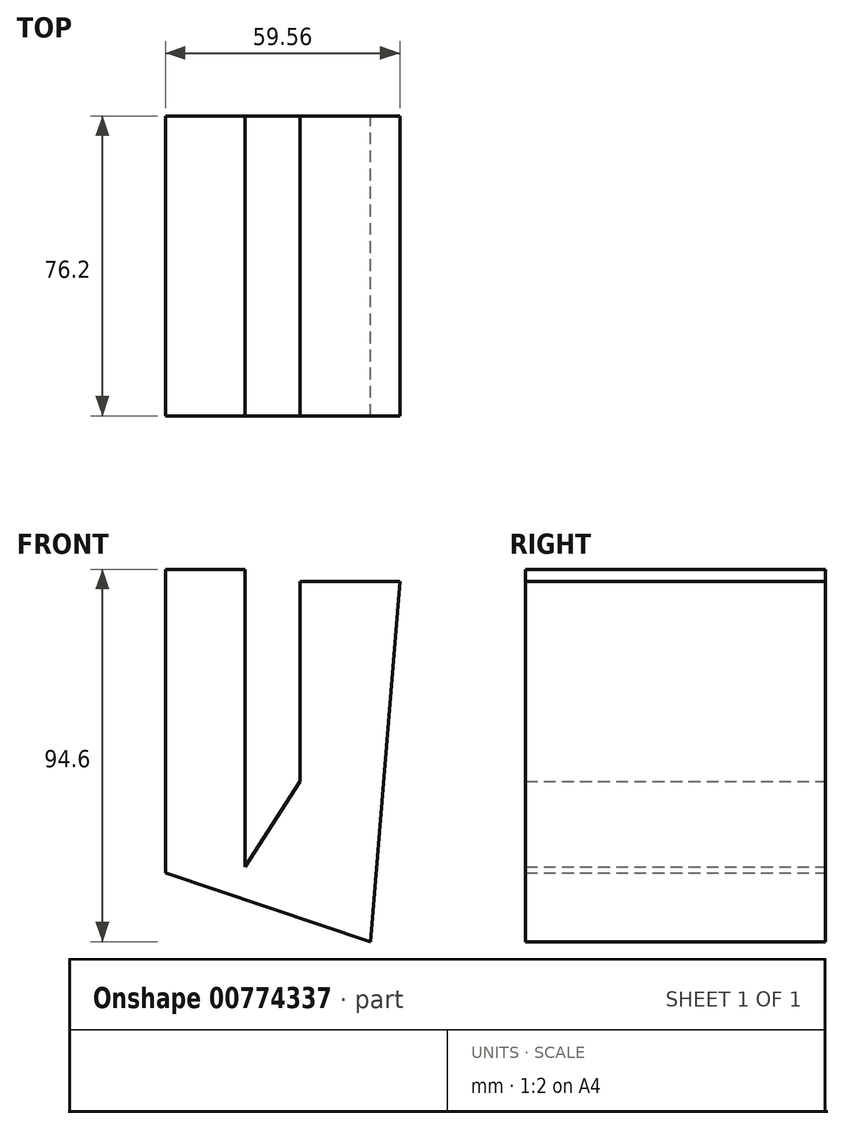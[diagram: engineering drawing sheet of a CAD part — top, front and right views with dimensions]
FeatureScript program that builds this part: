
annotation { "Feature Type Name" : "Feature", "Feature Type Description" : "" }
export const myFeature = defineFeature(function(context is Context, id is Id, definition is map)
    precondition{}
    {
        {
            var Q0;
            Q0=qCreatedBy(makeId("Front.planeOp"),FACE);
            var sketch = newSketch(context, id + "F0", { "sketchPlane" : qUnion([Q0])});
            skLineSegment(sketch, "E0", {"start": v(-68, -32.34) * mm, "end": v(-68, 44.83) * mm});
            skLineSegment(sketch, "E1", {"start": v(-68, 44.83) * mm, "end": v(-47.68, 44.83) * mm});
            skLineSegment(sketch, "E2", {"start": v(-47.68, 44.83) * mm, "end": v(-47.68, -30.8) * mm});
            skLineSegment(sketch, "E3", {"start": v(-33.84, 41.8) * mm, "end": v(-8.44, 41.8) * mm});
            skLineSegment(sketch, "E4", {"start": v(-33.84, 41.8) * mm, "end": v(-33.84, -9) * mm});
            skLineSegment(sketch, "E5", {"start": v(-47.68, -30.8) * mm, "end": v(-33.84, -9) * mm});
            skLineSegment(sketch, "E6", {"start": v(-8.44, 41.8) * mm, "end": v(-15.83, -49.77) * mm});
            skLineSegment(sketch, "E7", {"start": v(-15.83, -49.77) * mm, "end": v(-68, -32.34) * mm});
            skSolve(sketch);
        }
        {
            var Q0;
            Q0=makeQuery(id+"F0.imprint","IMPRINT",FACE,{"disambiguationData":[TD([[makeQuery(id+"F0.imprint","IMPRINT",EDGE,{"derivedFrom":sQuery(id+"F0.wireOp",EDGE,"E0")}),-1.0]])]});
            extrude(context, id + "F1", {"entities" : qUnion([Q0]), "depth" : 76.2 * mm, "offsetDistance" : 25.4 * mm});
        }
    });
